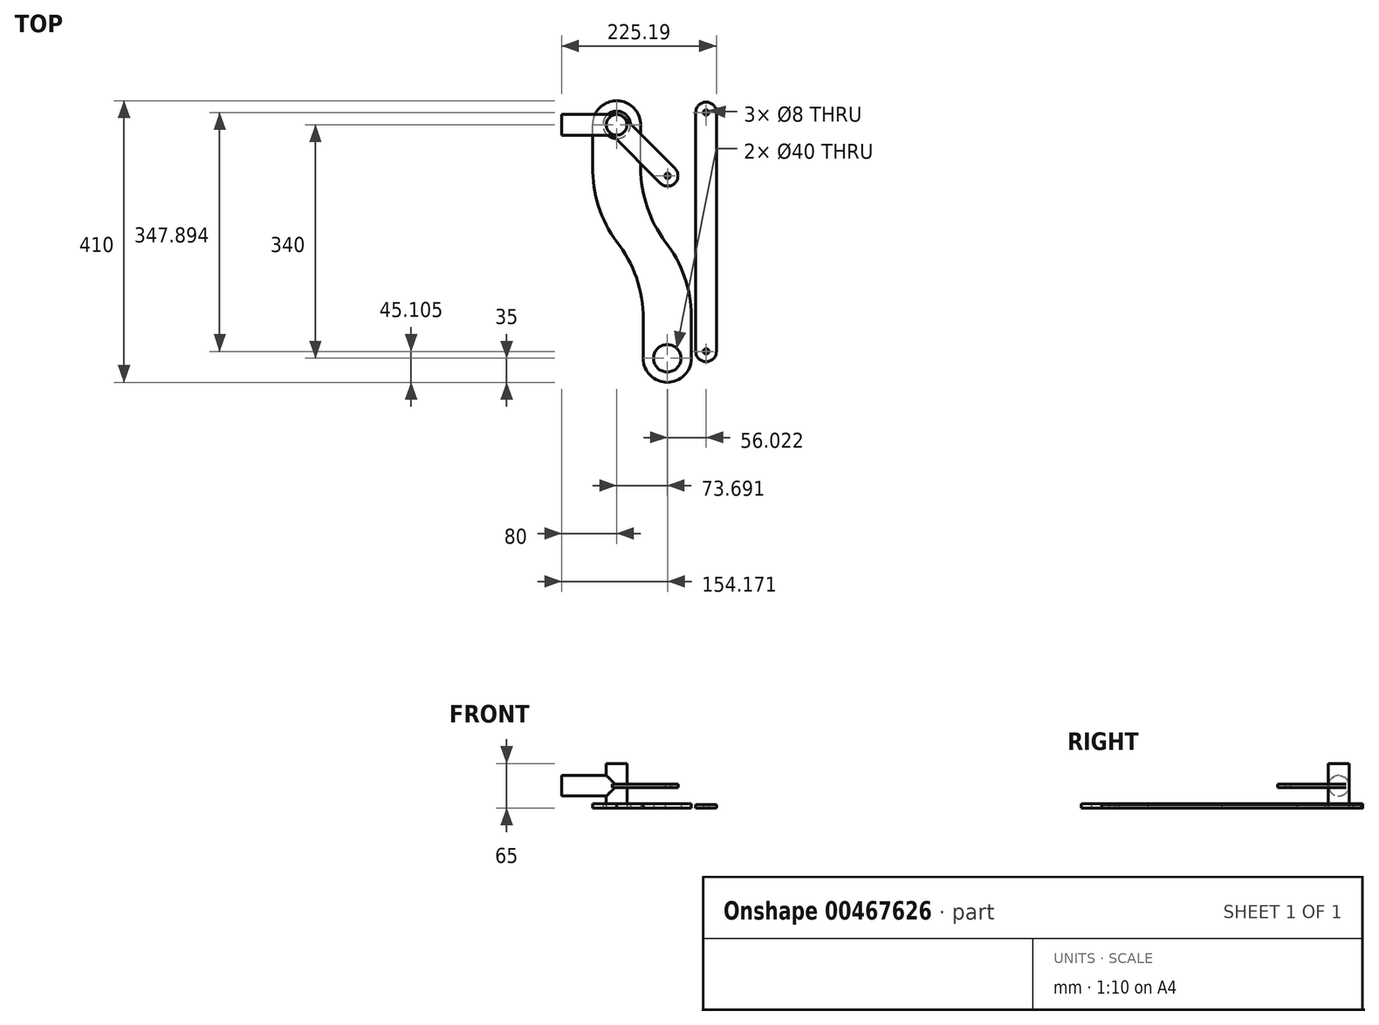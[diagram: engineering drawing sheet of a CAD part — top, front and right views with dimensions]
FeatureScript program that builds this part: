
annotation { "Feature Type Name" : "Feature", "Feature Type Description" : "" }
export const myFeature = defineFeature(function(context is Context, id is Id, definition is map)
    precondition{}
    {
        {
            var Q0;
            Q0=qCreatedBy(makeId("Top.planeOp"),FACE);
            var sketch = newSketch(context, id + "F0", { "sketchPlane" : qUnion([Q0])});
            skLineSegment(sketch, "E0.left", {"start": v(-35, -61.03) * mm, "end": v(-35, 0) * mm});
            skLineSegment(sketch, "E0.right", {"start": v(35, -63.52) * mm, "end": v(35, 0) * mm});
            skPoint(sketch, "E0.middle", {"position": v(0, 0) * mm});
            skCircle(sketch, "E1", {"center": v(0, 0) * mm, "radius": 20 * mm});
            skArc(sketch, "E2", {"start": v(-35, 0) * mm, "mid": v(0, 35) * mm, "end": v(35, 0) * mm});
            skPoint(sketch, "E3.orphan", {"position": v(-35, 122.34) * mm});
            skPoint(sketch, "E4.orphan", {"position": v(35, 122.34) * mm});
            skLineSegment(sketch, "E5.left", {"start": v(108.7, -278.31) * mm, "end": v(108.7, -340) * mm});
            skLineSegment(sketch, "E5.right", {"start": v(38.7, -280.3) * mm, "end": v(38.7, -340) * mm});
            skPoint(sketch, "E5.middle", {"position": v(73.7, -340) * mm});
            skCircle(sketch, "E6", {"center": v(73.7, -340) * mm, "radius": 20 * mm});
            skArc(sketch, "E7", {"start": v(108.7, -340) * mm, "mid": v(73.7, -375) * mm, "end": v(38.7, -340) * mm});
            skArc(sketch, "E8", {"start": v(-35, -61.03) * mm, "mid": v(-26.4, -118.37) * mm, "end": v(0, -170) * mm});
            skArc(sketch, "E9", {"start": v(38.7, -282.7) * mm, "mid": v(28.94, -223.06) * mm, "end": v(0, -170) * mm});
            skArc(sketch, "E10", {"start": v(108.7, -282.7) * mm, "mid": v(99.31, -223.13) * mm, "end": v(70.8, -170) * mm});
            skArc(sketch, "E11", {"start": v(35, -63.52) * mm, "mid": v(44.38, -119.62) * mm, "end": v(70.8, -170) * mm});
            skPoint(sketch, "E12.orphan", {"position": v(-35, -122.34) * mm});
            skPoint(sketch, "E13.orphan", {"position": v(35, -122.34) * mm});
            skPoint(sketch, "E14.orphan", {"position": v(35, -61.03) * mm});
            skSolve(sketch);
        }
        {
            var Q0;
            Q0=makeQuery(id+"F0.imprint","IMPRINT",FACE,{"disambiguationData":[TD([[makeQuery(id+"F0.imprint","IMPRINT",EDGE,{"derivedFrom":sQuery(id+"F0.wireOp",EDGE,"E0.left")}),-1.0]])]});
            extrude(context, id + "F1", {"entities" : qUnion([Q0]), "depth" : 6 * mm});
        }
        {
            var Q0;
            Q0=qCreatedBy(makeId("Top.planeOp"),FACE);
            var sketch = newSketch(context, id + "F2", { "sketchPlane" : qUnion([Q0])});
            skCircle(sketch, "E15", {"center": v(0, 0) * mm, "radius": 15 * mm});
            skSolve(sketch);
        }
        {
            var Q0;
            Q0 = qSketchRegion(id + "F2", true);
            extrude(context, id + "F3", {"entities" : qUnion([Q0]), "depth" : 65 * mm, "offsetDistance" : 25 * mm});
        }
        {
            var Q0;
            Q0=qCreatedBy(makeId("Right.planeOp"),FACE);
            var sketch = newSketch(context, id + "F4", { "sketchPlane" : qUnion([Q0])});
            skCircle(sketch, "E16", {"center": v(0, 32.5) * mm, "radius": 15 * mm});
            skSolve(sketch);
        }
        {
            var Q0;
            Q0 = qSketchRegion(id + "F4", true);
            extrude(context, id + "F5", {"entities" : qUnion([Q0]), "operationType" : NewBodyOperationType.ADD, "depth" : -80 * mm, "offsetDistance" : 25 * mm});
        }
        {
            var Q0;
            Q0=qCreatedBy(makeId("Front.planeOp"),FACE);
            var Q1;
            Q1=qCreatedBy(makeId("Right.planeOp"),FACE);
            cPlane(context, id + "F6", {"entities" : qUnion([Q0, Q1]), "cplaneType" : CPlaneType.MID_PLANE, "offset" : 25 * mm, "flipAlignment" : true, "width" : 150 * mm, "height" : 150 * mm});
        }
        {
            var Q0;
            Q0=qCreatedBy(id+"F6.planeOp",FACE);
            var sketch = newSketch(context, id + "F7", { "sketchPlane" : qUnion([Q0])});
            skLineSegment(sketch, "E17.bottom", {"start": v(15, 30) * mm, "end": v(-15, 30) * mm});
            skLineSegment(sketch, "E17.top", {"start": v(15, 35) * mm, "end": v(-15, 35) * mm});
            skLineSegment(sketch, "E17.left", {"start": v(15, 30) * mm, "end": v(15, 35) * mm});
            skLineSegment(sketch, "E17.right", {"start": v(-15, 30) * mm, "end": v(-15, 35) * mm});
            skPoint(sketch, "E17.middle", {"position": v(0, 32.5) * mm});
            skSolve(sketch);
        }
        {
            var Q0;
            Q0 = qSketchRegion(id + "F7", true);
            extrude(context, id + "F8", {"entities" : qUnion([Q0]), "operationType" : NewBodyOperationType.ADD, "depth" : 120 * mm, "offsetDistance" : 25 * mm});
        }
        {
            var Q0;
            Q0=qCreatedBy(makeId("Top.planeOp"),FACE);
            var sketch = newSketch(context, id + "F9", { "sketchPlane" : qUnion([Q0])});
            skPoint(sketch, "E18", {"position": v(74.17, -74.32) * mm});
            skSolve(sketch);
        }
        {
            var Q0;
            Q0=sQuery(id+"F9.wireOp",VERTEX,"E18");
            var Q1;
            Q1=makeQuery(id+"F3.opExtrude","SWEPT_BODY",BODY,{"disambiguationData":[OSD([sQuery(id+"F2.wireOp",EDGE,"E15")])]});
            hole(context, id + "F10", {"style" : HoleStyle.SIMPLE, "endStyle" : HoleEndStyle.THROUGH, "oppositeDirection" : true, "holeDiameter" : 8 * mm, "majorDiameter" : 5 * mm, "isTappedThrough" : true, "tappedDepth" : 12 * mm, "tapClearance" : 3, "locations" : qUnion([Q0]), "scope" : qUnion([Q1])});
        }
        {
            var Q0;
            Q0=makeQuery(id+"F8.opExtrude","CAP_EDGE",EDGE,{"disambiguationData":[OSD([sQuery(id+"F7.wireOp",EDGE,"E17.left")])],"isStart":false});
            var Q1;
            Q1=makeQuery(id+"F8.opExtrude","CAP_EDGE",EDGE,{"disambiguationData":[OSD([sQuery(id+"F7.wireOp",EDGE,"E17.right")])],"isStart":false});
            fillet(context, id + "F11", {"entities" : qUnion([Q0, Q1]), "radius" : 15 * mm, "tangentPropagation" : true, "allowEdgeOverflow" : false});
        }
        {
            var Q0;
            Q0=qCreatedBy(makeId("Top.planeOp"),FACE);
            var sketch = newSketch(context, id + "F12", { "sketchPlane" : qUnion([Q0])});
            skLineSegment(sketch, "E19.bottom", {"start": v(130.2, 33) * mm, "end": v(130.2, 33) * mm});
            skLineSegment(sketch, "E19.top", {"start": v(130.2, -344.9) * mm, "end": v(130.2, -344.9) * mm});
            skLineSegment(sketch, "E19.left", {"start": v(115.2, 18) * mm, "end": v(115.2, -329.9) * mm});
            skLineSegment(sketch, "E19.right", {"start": v(145.2, 18) * mm, "end": v(145.2, -329.9) * mm});
            skPoint(sketch, "E20", {"position": v(130.2, 18) * mm});
            skPoint(sketch, "E21", {"position": v(130.2, -329.9) * mm});
            skPoint(sketch, "E22.visualSharp", {"position": v(115.2, -344.9) * mm});
            skArc(sketch, "E22.filletArc", {"start": v(115.2, -329.9) * mm, "mid": v(119.59, -340.5) * mm, "end": v(130.2, -344.9) * mm});
            skPoint(sketch, "E23.visualSharp", {"position": v(145.2, -344.9) * mm});
            skArc(sketch, "E23.filletArc", {"start": v(130.2, -344.9) * mm, "mid": v(140.8, -340.5) * mm, "end": v(145.2, -329.9) * mm});
            skPoint(sketch, "E24.visualSharp", {"position": v(115.2, 33) * mm});
            skArc(sketch, "E24.filletArc", {"start": v(130.2, 33) * mm, "mid": v(119.59, 28.6) * mm, "end": v(115.2, 18) * mm});
            skPoint(sketch, "E25.visualSharp", {"position": v(145.2, 33) * mm});
            skArc(sketch, "E25.filletArc", {"start": v(145.2, 18) * mm, "mid": v(140.8, 28.6) * mm, "end": v(130.2, 33) * mm});
            skSolve(sketch);
        }
        {
            var Q0;
            Q0=makeQuery(id+"F12.imprint","IMPRINT",FACE,{"disambiguationData":[TD([[makeQuery(id+"F12.imprint","IMPRINT",EDGE,{"derivedFrom":sQuery(id+"F12.wireOp",EDGE,"E19.left")}),1.0]])]});
            extrude(context, id + "F13", {"entities" : qUnion([Q0]), "depth" : 5 * mm, "offsetDistance" : 25 * mm});
        }
        {
            var Q0;
            Q0=sQuery(id+"F12.wireOp",VERTEX,"E21");
            var Q1;
            Q1=sQuery(id+"F12.wireOp",VERTEX,"E20");
            var Q2;
            Q2=makeQuery(id+"F13.opExtrude","SWEPT_BODY",BODY,{"disambiguationData":[OSD([sQuery(id+"F12.wireOp",EDGE,"E19.left"),sQuery(id+"F12.wireOp",EDGE,"E19.right"),sQuery(id+"F12.wireOp",EDGE,"E22.filletArc"),sQuery(id+"F12.wireOp",EDGE,"E23.filletArc"),sQuery(id+"F12.wireOp",EDGE,"E24.filletArc"),sQuery(id+"F12.wireOp",EDGE,"E25.filletArc")])]});
            hole(context, id + "F14", {"style" : HoleStyle.SIMPLE, "endStyle" : HoleEndStyle.THROUGH, "oppositeDirection" : true, "holeDiameter" : 8 * mm, "majorDiameter" : 5 * mm, "isTappedThrough" : true, "tappedDepth" : 12 * mm, "tapClearance" : 3, "locations" : qUnion([Q0, Q1]), "scope" : qUnion([Q2])});
        }
    });
